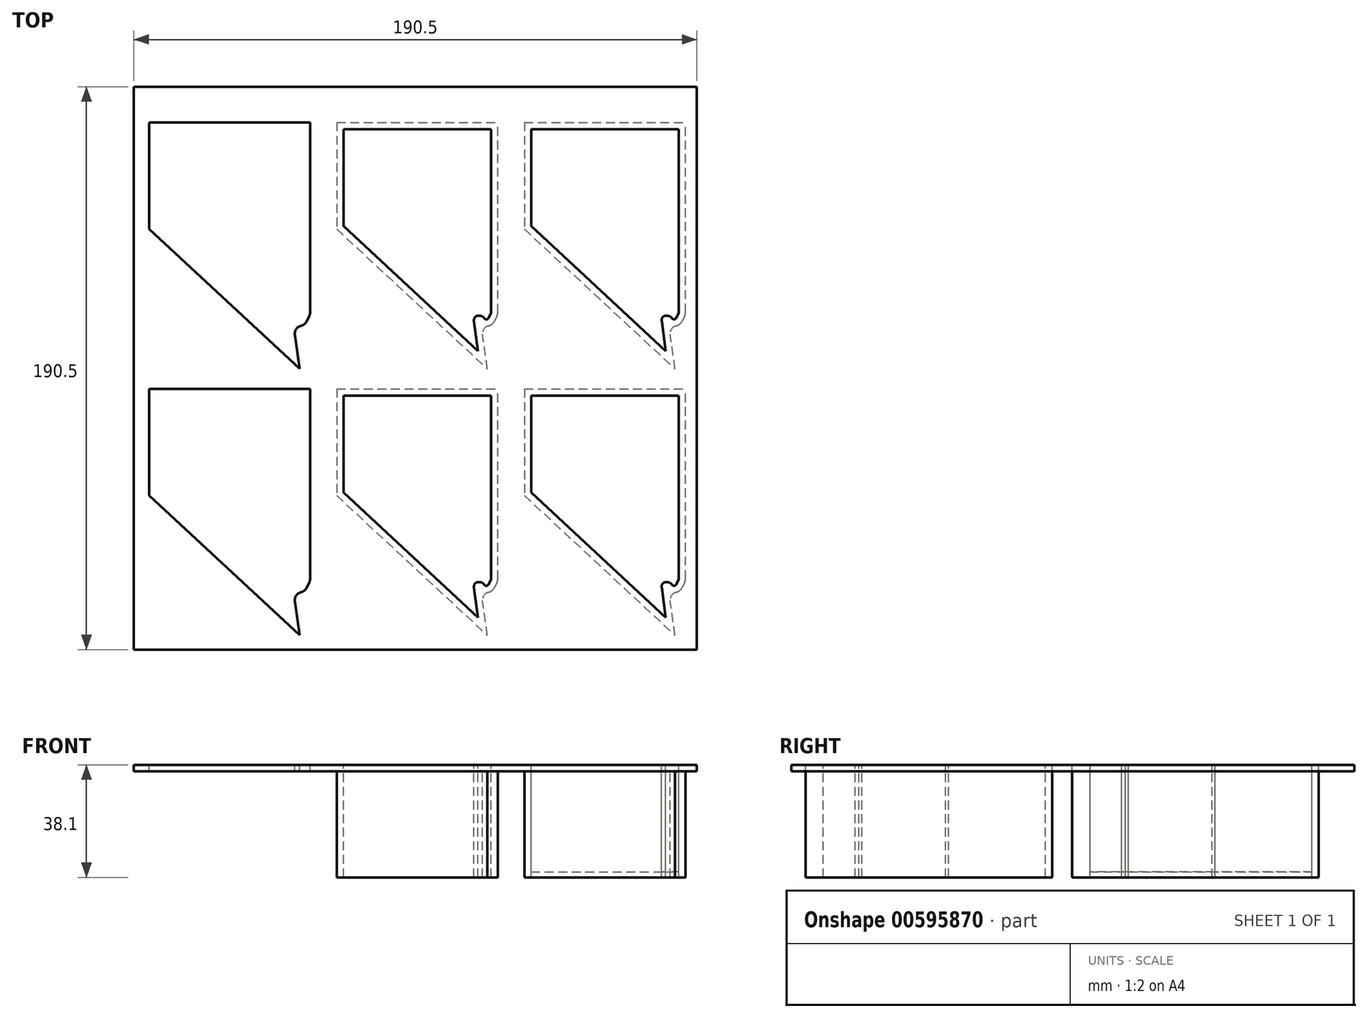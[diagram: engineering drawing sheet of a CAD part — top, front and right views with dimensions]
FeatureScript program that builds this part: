
annotation { "Feature Type Name" : "Feature", "Feature Type Description" : "" }
export const myFeature = defineFeature(function(context is Context, id is Id, definition is map)
    precondition{}
    {
        {
            var Q0;
            Q0=qCreatedBy(makeId("Top.planeOp"),FACE);
            var sketch = newSketch(context, id + "F0", { "sketchPlane" : qUnion([Q0])});
            skLineSegment(sketch, "E0.bottom", {"start": v(-114.3, -95.25) * mm, "end": v(76.2, -95.25) * mm});
            skLineSegment(sketch, "E0.top", {"start": v(-114.3, 95.25) * mm, "end": v(76.2, 95.25) * mm});
            skLineSegment(sketch, "E0.left", {"start": v(-114.3, -95.25) * mm, "end": v(-114.3, 95.25) * mm});
            skLineSegment(sketch, "E0.right", {"start": v(76.2, -95.25) * mm, "end": v(76.2, 95.25) * mm});
            skLineSegment(sketch, "E1", {"start": v(20.1, 80.88) * mm, "end": v(20.1, 48.05) * mm});
            skLineSegment(sketch, "E2", {"start": v(65.66, 5.75) * mm, "end": v(64.3, 16.05) * mm});
            skLineSegment(sketch, "E3", {"start": v(70.06, 18.75) * mm, "end": v(70.06, 80.88) * mm});
            skLineSegment(sketch, "E4", {"start": v(20.1, 80.88) * mm, "end": v(70.06, 80.88) * mm});
            skLineSegment(sketch, "E5", {"start": v(20.1, 48.05) * mm, "end": v(65.66, 5.75) * mm});
            skLineSegment(sketch, "E6", {"start": v(65.58, 17.73) * mm, "end": v(65.7, 17.75) * mm});
            skLineSegment(sketch, "E7", {"start": v(67.72, 17) * mm, "end": v(67.97, 16.73) * mm});
            skLineSegment(sketch, "E8", {"start": v(70.06, 18.75) * mm, "end": v(69.13, 16.89) * mm});
            skPoint(sketch, "E9.visualSharp", {"position": v(64.1, 17.54) * mm});
            skArc(sketch, "E9.filletArc", {"start": v(65.58, 17.73) * mm, "mid": v(64.6, 17.16) * mm, "end": v(64.3, 16.05) * mm});
            skPoint(sketch, "E10.visualSharp", {"position": v(66.9, 17.9) * mm});
            skArc(sketch, "E10.filletArc", {"start": v(67.72, 17) * mm, "mid": v(66.8, 17.62) * mm, "end": v(65.7, 17.75) * mm});
            skPoint(sketch, "E11.visualSharp", {"position": v(68.67, 15.95) * mm});
            skArc(sketch, "E11.filletArc", {"start": v(67.97, 16.73) * mm, "mid": v(68.6, 16.5) * mm, "end": v(69.13, 16.89) * mm});
            skLineSegment(sketch, "E12.0", {"start": v(17.82, 47.06) * mm, "end": v(68.76, -0.25) * mm});
            skLineSegment(sketch, "E12.1", {"start": v(17.82, 83.17) * mm, "end": v(17.82, 47.06) * mm});
            skArc(sketch, "E12.2", {"start": v(69.16, 14.28) * mm, "mid": v(70.35, 14.85) * mm, "end": v(71.18, 15.87) * mm});
            skLineSegment(sketch, "E12.3", {"start": v(72.08, 17.68) * mm, "end": v(71.18, 15.87) * mm});
            skLineSegment(sketch, "E12.4", {"start": v(72.34, 18.81) * mm, "end": v(72.34, 83.17) * mm});
            skLineSegment(sketch, "E12.5", {"start": v(68.76, -0.25) * mm, "end": v(67.21, 11.47) * mm});
            skLineSegment(sketch, "E12.6", {"start": v(17.82, 83.17) * mm, "end": v(72.34, 83.17) * mm});
            skPoint(sketch, "E13.visualSharp", {"position": v(66.78, 14.75) * mm});
            skArc(sketch, "E13.filletArc", {"start": v(69.16, 14.28) * mm, "mid": v(67.64, 13.26) * mm, "end": v(67.21, 11.47) * mm});
            skPoint(sketch, "E14.visualSharp", {"position": v(72.34, 18.22) * mm});
            skArc(sketch, "E14.filletArc", {"start": v(72.08, 17.68) * mm, "mid": v(72.28, 18.23) * mm, "end": v(72.34, 18.81) * mm});
            skLineSegment(sketch, "E15.0.1.0", {"start": v(20.1, -42.12) * mm, "end": v(65.66, -84.42) * mm});
            skLineSegment(sketch, "E15.0.1.1", {"start": v(70.06, -71.42) * mm, "end": v(70.06, -9.29) * mm});
            skLineSegment(sketch, "E15.0.1.2", {"start": v(20.1, -9.29) * mm, "end": v(20.1, -42.12) * mm});
            skLineSegment(sketch, "E15.0.1.3", {"start": v(72.34, -71.36) * mm, "end": v(72.34, -7) * mm});
            skLineSegment(sketch, "E15.0.1.4", {"start": v(17.82, -7) * mm, "end": v(72.34, -7) * mm});
            skLineSegment(sketch, "E15.0.1.5", {"start": v(17.82, -7) * mm, "end": v(17.82, -43.11) * mm});
            skLineSegment(sketch, "E15.0.1.6", {"start": v(20.1, -9.29) * mm, "end": v(70.06, -9.29) * mm});
            skLineSegment(sketch, "E15.0.1.7", {"start": v(17.82, -43.11) * mm, "end": v(68.76, -90.42) * mm});
            skLineSegment(sketch, "E15.0.1.8", {"start": v(68.76, -90.42) * mm, "end": v(67.21, -78.7) * mm});
            skPoint(sketch, "E15.0.1.9", {"position": v(66.78, -75.42) * mm});
            skPoint(sketch, "E15.0.1.10", {"position": v(64.1, -72.63) * mm});
            skLineSegment(sketch, "E15.0.1.11", {"start": v(65.66, -84.42) * mm, "end": v(64.3, -74.12) * mm});
            skPoint(sketch, "E15.0.1.12", {"position": v(66.9, -72.26) * mm});
            skPoint(sketch, "E15.0.1.13", {"position": v(68.67, -74.22) * mm});
            skPoint(sketch, "E15.0.1.14", {"position": v(72.34, -71.95) * mm});
            skArc(sketch, "E15.0.1.15", {"start": v(69.16, -75.89) * mm, "mid": v(67.64, -76.91) * mm, "end": v(67.21, -78.7) * mm});
            skArc(sketch, "E15.0.1.16", {"start": v(72.08, -72.49) * mm, "mid": v(72.28, -71.94) * mm, "end": v(72.34, -71.36) * mm});
            skLineSegment(sketch, "E15.0.1.17", {"start": v(72.08, -72.49) * mm, "end": v(71.18, -74.3) * mm});
            skArc(sketch, "E15.0.1.18", {"start": v(69.16, -75.89) * mm, "mid": v(70.35, -75.32) * mm, "end": v(71.18, -74.3) * mm});
            skLineSegment(sketch, "E15.0.1.19", {"start": v(67.72, -73.17) * mm, "end": v(67.97, -73.44) * mm});
            skLineSegment(sketch, "E15.0.1.20", {"start": v(70.06, -71.42) * mm, "end": v(69.13, -73.28) * mm});
            skArc(sketch, "E15.0.1.21", {"start": v(67.97, -73.44) * mm, "mid": v(68.6, -73.67) * mm, "end": v(69.13, -73.28) * mm});
            skArc(sketch, "E15.0.1.22", {"start": v(67.72, -73.17) * mm, "mid": v(66.8, -72.55) * mm, "end": v(65.7, -72.42) * mm});
            skArc(sketch, "E15.0.1.23", {"start": v(65.58, -72.44) * mm, "mid": v(64.6, -73.01) * mm, "end": v(64.3, -74.12) * mm});
            skLineSegment(sketch, "E15.0.1.24", {"start": v(65.58, -72.44) * mm, "end": v(65.7, -72.42) * mm});
            skLineSegment(sketch, "E15.1.0.0", {"start": v(-43.4, 48.05) * mm, "end": v(2.16, 5.75) * mm});
            skLineSegment(sketch, "E15.1.0.1", {"start": v(6.56, 18.75) * mm, "end": v(6.56, 80.88) * mm});
            skLineSegment(sketch, "E15.1.0.2", {"start": v(-43.4, 80.88) * mm, "end": v(-43.4, 48.05) * mm});
            skLineSegment(sketch, "E15.1.0.3", {"start": v(8.84, 18.81) * mm, "end": v(8.84, 83.17) * mm});
            skLineSegment(sketch, "E15.1.0.4", {"start": v(-45.68, 83.17) * mm, "end": v(8.84, 83.17) * mm});
            skLineSegment(sketch, "E15.1.0.5", {"start": v(-45.68, 83.17) * mm, "end": v(-45.68, 47.06) * mm});
            skLineSegment(sketch, "E15.1.0.6", {"start": v(-43.4, 80.88) * mm, "end": v(6.56, 80.88) * mm});
            skLineSegment(sketch, "E15.1.0.7", {"start": v(-45.68, 47.06) * mm, "end": v(5.26, -0.25) * mm});
            skLineSegment(sketch, "E15.1.0.8", {"start": v(5.26, -0.25) * mm, "end": v(3.71, 11.47) * mm});
            skPoint(sketch, "E15.1.0.9", {"position": v(3.28, 14.75) * mm});
            skPoint(sketch, "E15.1.0.10", {"position": v(0.6, 17.54) * mm});
            skLineSegment(sketch, "E15.1.0.11", {"start": v(2.16, 5.75) * mm, "end": v(0.8, 16.05) * mm});
            skPoint(sketch, "E15.1.0.12", {"position": v(3.4, 17.9) * mm});
            skPoint(sketch, "E15.1.0.13", {"position": v(5.17, 15.95) * mm});
            skPoint(sketch, "E15.1.0.14", {"position": v(8.84, 18.22) * mm});
            skArc(sketch, "E15.1.0.15", {"start": v(5.66, 14.28) * mm, "mid": v(4.14, 13.26) * mm, "end": v(3.71, 11.47) * mm});
            skArc(sketch, "E15.1.0.16", {"start": v(8.58, 17.68) * mm, "mid": v(8.78, 18.23) * mm, "end": v(8.84, 18.81) * mm});
            skLineSegment(sketch, "E15.1.0.17", {"start": v(8.58, 17.68) * mm, "end": v(7.68, 15.87) * mm});
            skArc(sketch, "E15.1.0.18", {"start": v(5.66, 14.28) * mm, "mid": v(6.85, 14.85) * mm, "end": v(7.68, 15.87) * mm});
            skLineSegment(sketch, "E15.1.0.19", {"start": v(4.22, 17) * mm, "end": v(4.47, 16.73) * mm});
            skLineSegment(sketch, "E15.1.0.20", {"start": v(6.56, 18.75) * mm, "end": v(5.63, 16.89) * mm});
            skArc(sketch, "E15.1.0.21", {"start": v(4.47, 16.73) * mm, "mid": v(5.1, 16.5) * mm, "end": v(5.63, 16.89) * mm});
            skArc(sketch, "E15.1.0.22", {"start": v(4.22, 17) * mm, "mid": v(3.3, 17.62) * mm, "end": v(2.2, 17.75) * mm});
            skArc(sketch, "E15.1.0.23", {"start": v(2.08, 17.73) * mm, "mid": v(1.1, 17.16) * mm, "end": v(0.8, 16.05) * mm});
            skLineSegment(sketch, "E15.1.0.24", {"start": v(2.08, 17.73) * mm, "end": v(2.2, 17.75) * mm});
            skLineSegment(sketch, "E15.1.1.0", {"start": v(-43.4, -42.12) * mm, "end": v(2.16, -84.42) * mm});
            skLineSegment(sketch, "E15.1.1.1", {"start": v(6.56, -71.42) * mm, "end": v(6.56, -9.29) * mm});
            skLineSegment(sketch, "E15.1.1.2", {"start": v(-43.4, -9.29) * mm, "end": v(-43.4, -42.12) * mm});
            skLineSegment(sketch, "E15.1.1.3", {"start": v(8.84, -71.36) * mm, "end": v(8.84, -7) * mm});
            skLineSegment(sketch, "E15.1.1.4", {"start": v(-45.68, -7) * mm, "end": v(8.84, -7) * mm});
            skLineSegment(sketch, "E15.1.1.5", {"start": v(-45.68, -7) * mm, "end": v(-45.68, -43.11) * mm});
            skLineSegment(sketch, "E15.1.1.6", {"start": v(-43.4, -9.29) * mm, "end": v(6.56, -9.29) * mm});
            skLineSegment(sketch, "E15.1.1.7", {"start": v(-45.68, -43.11) * mm, "end": v(5.26, -90.42) * mm});
            skLineSegment(sketch, "E15.1.1.8", {"start": v(5.26, -90.42) * mm, "end": v(3.71, -78.7) * mm});
            skPoint(sketch, "E15.1.1.9", {"position": v(3.28, -75.42) * mm});
            skPoint(sketch, "E15.1.1.10", {"position": v(0.6, -72.63) * mm});
            skLineSegment(sketch, "E15.1.1.11", {"start": v(2.16, -84.42) * mm, "end": v(0.8, -74.12) * mm});
            skPoint(sketch, "E15.1.1.12", {"position": v(3.4, -72.26) * mm});
            skPoint(sketch, "E15.1.1.13", {"position": v(5.17, -74.22) * mm});
            skPoint(sketch, "E15.1.1.14", {"position": v(8.84, -71.95) * mm});
            skArc(sketch, "E15.1.1.15", {"start": v(5.66, -75.89) * mm, "mid": v(4.14, -76.91) * mm, "end": v(3.71, -78.7) * mm});
            skArc(sketch, "E15.1.1.16", {"start": v(8.58, -72.49) * mm, "mid": v(8.78, -71.94) * mm, "end": v(8.84, -71.36) * mm});
            skLineSegment(sketch, "E15.1.1.17", {"start": v(8.58, -72.49) * mm, "end": v(7.68, -74.3) * mm});
            skArc(sketch, "E15.1.1.18", {"start": v(5.66, -75.89) * mm, "mid": v(6.85, -75.32) * mm, "end": v(7.68, -74.3) * mm});
            skLineSegment(sketch, "E15.1.1.19", {"start": v(4.22, -73.17) * mm, "end": v(4.47, -73.44) * mm});
            skLineSegment(sketch, "E15.1.1.20", {"start": v(6.56, -71.42) * mm, "end": v(5.63, -73.28) * mm});
            skArc(sketch, "E15.1.1.21", {"start": v(4.47, -73.44) * mm, "mid": v(5.1, -73.67) * mm, "end": v(5.63, -73.28) * mm});
            skArc(sketch, "E15.1.1.22", {"start": v(4.22, -73.17) * mm, "mid": v(3.3, -72.55) * mm, "end": v(2.2, -72.42) * mm});
            skArc(sketch, "E15.1.1.23", {"start": v(2.08, -72.44) * mm, "mid": v(1.1, -73.01) * mm, "end": v(0.8, -74.12) * mm});
            skLineSegment(sketch, "E15.1.1.24", {"start": v(2.08, -72.44) * mm, "end": v(2.2, -72.42) * mm});
            skLineSegment(sketch, "E15.direction1", {"start": v(17.82, 47.06) * mm, "end": v(-45.68, 47.06) * mm, "construction": true});
            skLineSegment(sketch, "E15.direction2", {"start": v(17.82, 47.06) * mm, "end": v(17.82, -43.11) * mm, "construction": true});
            skLineSegment(sketch, "E16.0.2.0", {"start": v(-106.9, 48.05) * mm, "end": v(-61.34, 5.75) * mm});
            skLineSegment(sketch, "E16.3.2.0", {"start": v(-56.94, 18.75) * mm, "end": v(-56.94, 80.88) * mm});
            skLineSegment(sketch, "E16.6.2.0", {"start": v(-106.9, 80.88) * mm, "end": v(-106.9, 48.05) * mm});
            skLineSegment(sketch, "E16.9.2.0", {"start": v(-54.66, 18.81) * mm, "end": v(-54.66, 83.17) * mm});
            skLineSegment(sketch, "E16.12.2.0", {"start": v(-109.18, 83.17) * mm, "end": v(-54.66, 83.17) * mm});
            skLineSegment(sketch, "E16.15.2.0", {"start": v(-109.18, 83.17) * mm, "end": v(-109.18, 47.06) * mm});
            skLineSegment(sketch, "E16.18.2.0", {"start": v(-106.9, 80.88) * mm, "end": v(-56.94, 80.88) * mm});
            skLineSegment(sketch, "E16.21.2.0", {"start": v(-109.18, 47.06) * mm, "end": v(-58.24, -0.25) * mm});
            skLineSegment(sketch, "E16.24.2.0", {"start": v(-58.24, -0.25) * mm, "end": v(-59.79, 11.47) * mm});
            skPoint(sketch, "E16.27.2.0", {"position": v(-60.22, 14.75) * mm});
            skPoint(sketch, "E16.28.2.0", {"position": v(-62.9, 17.54) * mm});
            skLineSegment(sketch, "E16.29.2.0", {"start": v(-61.34, 5.75) * mm, "end": v(-62.7, 16.05) * mm});
            skPoint(sketch, "E16.32.2.0", {"position": v(-60.1, 17.9) * mm});
            skPoint(sketch, "E16.33.2.0", {"position": v(-58.33, 15.95) * mm});
            skPoint(sketch, "E16.34.2.0", {"position": v(-54.66, 18.22) * mm});
            skArc(sketch, "E16.35.2.0", {"start": v(-57.84, 14.28) * mm, "mid": v(-59.36, 13.26) * mm, "end": v(-59.79, 11.47) * mm});
            skArc(sketch, "E16.39.2.0", {"start": v(-54.92, 17.68) * mm, "mid": v(-54.72, 18.23) * mm, "end": v(-54.66, 18.81) * mm});
            skLineSegment(sketch, "E16.43.2.0", {"start": v(-54.92, 17.68) * mm, "end": v(-55.82, 15.87) * mm});
            skArc(sketch, "E16.46.2.0", {"start": v(-57.84, 14.28) * mm, "mid": v(-56.65, 14.85) * mm, "end": v(-55.82, 15.87) * mm});
            skLineSegment(sketch, "E16.50.2.0", {"start": v(-59.28, 17) * mm, "end": v(-59.03, 16.73) * mm});
            skLineSegment(sketch, "E16.53.2.0", {"start": v(-56.94, 18.75) * mm, "end": v(-57.87, 16.89) * mm});
            skArc(sketch, "E16.56.2.0", {"start": v(-59.03, 16.73) * mm, "mid": v(-58.4, 16.5) * mm, "end": v(-57.87, 16.89) * mm});
            skArc(sketch, "E16.60.2.0", {"start": v(-59.28, 17) * mm, "mid": v(-60.2, 17.62) * mm, "end": v(-61.3, 17.75) * mm});
            skArc(sketch, "E16.64.2.0", {"start": v(-61.42, 17.73) * mm, "mid": v(-62.4, 17.16) * mm, "end": v(-62.7, 16.05) * mm});
            skLineSegment(sketch, "E16.68.2.0", {"start": v(-61.42, 17.73) * mm, "end": v(-61.3, 17.75) * mm});
            skLineSegment(sketch, "E16.0.2.1", {"start": v(-106.9, -42.12) * mm, "end": v(-61.34, -84.42) * mm});
            skLineSegment(sketch, "E16.3.2.1", {"start": v(-56.94, -71.42) * mm, "end": v(-56.94, -9.29) * mm});
            skLineSegment(sketch, "E16.6.2.1", {"start": v(-106.9, -9.29) * mm, "end": v(-106.9, -42.12) * mm});
            skLineSegment(sketch, "E16.9.2.1", {"start": v(-54.66, -71.36) * mm, "end": v(-54.66, -7) * mm});
            skLineSegment(sketch, "E16.12.2.1", {"start": v(-109.18, -7) * mm, "end": v(-54.66, -7) * mm});
            skLineSegment(sketch, "E16.15.2.1", {"start": v(-109.18, -7) * mm, "end": v(-109.18, -43.11) * mm});
            skLineSegment(sketch, "E16.18.2.1", {"start": v(-106.9, -9.29) * mm, "end": v(-56.94, -9.29) * mm});
            skLineSegment(sketch, "E16.21.2.1", {"start": v(-109.18, -43.11) * mm, "end": v(-58.24, -90.42) * mm});
            skLineSegment(sketch, "E16.24.2.1", {"start": v(-58.24, -90.42) * mm, "end": v(-59.79, -78.7) * mm});
            skPoint(sketch, "E16.27.2.1", {"position": v(-60.22, -75.42) * mm});
            skPoint(sketch, "E16.28.2.1", {"position": v(-62.9, -72.63) * mm});
            skLineSegment(sketch, "E16.29.2.1", {"start": v(-61.34, -84.42) * mm, "end": v(-62.7, -74.12) * mm});
            skPoint(sketch, "E16.32.2.1", {"position": v(-60.1, -72.26) * mm});
            skPoint(sketch, "E16.33.2.1", {"position": v(-58.33, -74.22) * mm});
            skPoint(sketch, "E16.34.2.1", {"position": v(-54.66, -71.95) * mm});
            skArc(sketch, "E16.35.2.1", {"start": v(-57.84, -75.89) * mm, "mid": v(-59.36, -76.91) * mm, "end": v(-59.79, -78.7) * mm});
            skArc(sketch, "E16.39.2.1", {"start": v(-54.92, -72.49) * mm, "mid": v(-54.72, -71.94) * mm, "end": v(-54.66, -71.36) * mm});
            skLineSegment(sketch, "E16.43.2.1", {"start": v(-54.92, -72.49) * mm, "end": v(-55.82, -74.3) * mm});
            skArc(sketch, "E16.46.2.1", {"start": v(-57.84, -75.89) * mm, "mid": v(-56.65, -75.32) * mm, "end": v(-55.82, -74.3) * mm});
            skLineSegment(sketch, "E16.50.2.1", {"start": v(-59.28, -73.17) * mm, "end": v(-59.03, -73.44) * mm});
            skLineSegment(sketch, "E16.53.2.1", {"start": v(-56.94, -71.42) * mm, "end": v(-57.87, -73.28) * mm});
            skArc(sketch, "E16.56.2.1", {"start": v(-59.03, -73.44) * mm, "mid": v(-58.4, -73.67) * mm, "end": v(-57.87, -73.28) * mm});
            skArc(sketch, "E16.60.2.1", {"start": v(-59.28, -73.17) * mm, "mid": v(-60.2, -72.55) * mm, "end": v(-61.3, -72.42) * mm});
            skArc(sketch, "E16.64.2.1", {"start": v(-61.42, -72.44) * mm, "mid": v(-62.4, -73.01) * mm, "end": v(-62.7, -74.12) * mm});
            skLineSegment(sketch, "E16.68.2.1", {"start": v(-61.42, -72.44) * mm, "end": v(-61.3, -72.42) * mm});
            skSolve(sketch);
        }
        {
            var Q0;
            Q0=makeQuery(id+"F0.imprint","IMPRINT",FACE,{"disambiguationData":[TD([[makeQuery(id+"F0.imprint","IMPRINT",EDGE,{"derivedFrom":sQuery(id+"F0.wireOp",EDGE,"E15.0.1.0")}),-1.0]])]});
            var Q1;
            Q1=makeQuery(id+"F0.imprint","IMPRINT",FACE,{"disambiguationData":[TD([[makeQuery(id+"F0.imprint","IMPRINT",EDGE,{"derivedFrom":sQuery(id+"F0.wireOp",EDGE,"E1")}),-1.0]])]});
            var Q2;
            Q2=makeQuery(id+"F0.imprint","IMPRINT",FACE,{"disambiguationData":[TD([[makeQuery(id+"F0.imprint","IMPRINT",EDGE,{"derivedFrom":sQuery(id+"F0.wireOp",EDGE,"E15.1.0.0")}),-1.0]])]});
            var Q3;
            Q3=makeQuery(id+"F0.imprint","IMPRINT",FACE,{"disambiguationData":[TD([[makeQuery(id+"F0.imprint","IMPRINT",EDGE,{"derivedFrom":sQuery(id+"F0.wireOp",EDGE,"E15.1.1.0")}),-1.0]])]});
            extrude(context, id + "F1", {"entities" : qUnion([Q0, Q1, Q2, Q3]), "oppositeDirection" : true, "depth" : 38.1 * mm, "offsetDistance" : 25.4 * mm});
        }
        {
            var Q0;
            Q0=makeQuery(id+"F0.imprint","IMPRINT",FACE,{"disambiguationData":[TD([[makeQuery(id+"F0.imprint","IMPRINT",EDGE,{"derivedFrom":sQuery(id+"F0.wireOp",EDGE,"E0.bottom")}),1.0]])]});
            extrude(context, id + "F2", {"entities" : qUnion([Q0]), "operationType" : NewBodyOperationType.ADD, "oppositeDirection" : true, "depth" : 2.16 * mm, "offsetDistance" : 25.4 * mm});
        }
        {
            var Q0;
            Q0=makeQuery(id+"F1.opExtrude","CAP_FACE",FACE,{"disambiguationData":[OSD([sQuery(id+"F0.wireOp",EDGE,"E1"),sQuery(id+"F0.wireOp",EDGE,"E2"),sQuery(id+"F0.wireOp",EDGE,"E3"),sQuery(id+"F0.wireOp",EDGE,"E4"),sQuery(id+"F0.wireOp",EDGE,"E5"),sQuery(id+"F0.wireOp",EDGE,"E6"),sQuery(id+"F0.wireOp",EDGE,"E7"),sQuery(id+"F0.wireOp",EDGE,"E8"),sQuery(id+"F0.wireOp",EDGE,"E9.filletArc"),sQuery(id+"F0.wireOp",EDGE,"E10.filletArc"),sQuery(id+"F0.wireOp",EDGE,"E11.filletArc"),sQuery(id+"F0.wireOp",EDGE,"E12.0"),sQuery(id+"F0.wireOp",EDGE,"E12.1"),sQuery(id+"F0.wireOp",EDGE,"E12.2"),sQuery(id+"F0.wireOp",EDGE,"E12.3"),sQuery(id+"F0.wireOp",EDGE,"E12.4"),sQuery(id+"F0.wireOp",EDGE,"E12.5"),sQuery(id+"F0.wireOp",EDGE,"E12.6"),sQuery(id+"F0.wireOp",EDGE,"E13.filletArc"),sQuery(id+"F0.wireOp",EDGE,"E14.filletArc")])],"isStart":false});
            cPlane(context, id + "F3", {"entities" : qUnion([Q0]), "cplaneType" : CPlaneType.OFFSET, "offset" : 0 * mm, "width" : 152.4 * mm, "height" : 152.4 * mm});
        }
        {
            var Q0;
            Q0=qCreatedBy(id+"F3.planeOp",FACE);
            var sketch = newSketch(context, id + "F4", { "sketchPlane" : qUnion([Q0])});
            skLineSegment(sketch, "E17.0.0", {"start": v(72.08, -17.68) * mm, "end": v(71.18, -15.87) * mm});
            skArc(sketch, "E17.0.1", {"start": v(71.18, -15.87) * mm, "mid": v(70.35, -14.85) * mm, "end": v(69.16, -14.28) * mm});
            skArc(sketch, "E17.0.2", {"start": v(69.16, -14.28) * mm, "mid": v(67.64, -13.26) * mm, "end": v(67.21, -11.47) * mm});
            skLineSegment(sketch, "E17.0.3", {"start": v(67.21, -11.47) * mm, "end": v(68.76, 0.25) * mm});
            skLineSegment(sketch, "E17.0.4", {"start": v(68.76, 0.25) * mm, "end": v(17.82, -47.06) * mm});
            skLineSegment(sketch, "E17.0.5", {"start": v(17.82, -47.06) * mm, "end": v(17.82, -83.17) * mm});
            skLineSegment(sketch, "E17.0.6", {"start": v(17.82, -83.17) * mm, "end": v(72.34, -83.17) * mm});
            skLineSegment(sketch, "E17.0.7", {"start": v(72.34, -83.17) * mm, "end": v(72.34, -18.81) * mm});
            skArc(sketch, "E17.0.8", {"start": v(72.34, -18.81) * mm, "mid": v(72.28, -18.23) * mm, "end": v(72.08, -17.68) * mm});
            skArc(sketch, "E18.0.0", {"start": v(5.66, -14.28) * mm, "mid": v(4.14, -13.26) * mm, "end": v(3.71, -11.47) * mm});
            skLineSegment(sketch, "E18.0.1", {"start": v(3.71, -11.47) * mm, "end": v(5.26, 0.25) * mm});
            skLineSegment(sketch, "E18.0.2", {"start": v(5.26, 0.25) * mm, "end": v(-45.68, -47.06) * mm});
            skLineSegment(sketch, "E18.0.3", {"start": v(-45.68, -47.06) * mm, "end": v(-45.68, -83.17) * mm});
            skLineSegment(sketch, "E18.0.4", {"start": v(-45.68, -83.17) * mm, "end": v(8.84, -83.17) * mm});
            skLineSegment(sketch, "E18.0.5", {"start": v(8.84, -83.17) * mm, "end": v(8.84, -18.81) * mm});
            skArc(sketch, "E18.0.6", {"start": v(8.84, -18.81) * mm, "mid": v(8.78, -18.23) * mm, "end": v(8.58, -17.68) * mm});
            skLineSegment(sketch, "E18.0.7", {"start": v(8.58, -17.68) * mm, "end": v(7.68, -15.87) * mm});
            skArc(sketch, "E18.0.8", {"start": v(7.68, -15.87) * mm, "mid": v(6.85, -14.85) * mm, "end": v(5.66, -14.28) * mm});
            skArc(sketch, "E19.0.0", {"start": v(5.66, 75.89) * mm, "mid": v(4.14, 76.91) * mm, "end": v(3.71, 78.7) * mm});
            skLineSegment(sketch, "E19.0.1", {"start": v(3.71, 78.7) * mm, "end": v(5.26, 90.42) * mm});
            skLineSegment(sketch, "E19.0.2", {"start": v(5.26, 90.42) * mm, "end": v(-45.68, 43.11) * mm});
            skLineSegment(sketch, "E19.0.3", {"start": v(-45.68, 43.11) * mm, "end": v(-45.68, 7) * mm});
            skLineSegment(sketch, "E19.0.4", {"start": v(-45.68, 7) * mm, "end": v(8.84, 7) * mm});
            skLineSegment(sketch, "E19.0.5", {"start": v(8.84, 7) * mm, "end": v(8.84, 71.36) * mm});
            skArc(sketch, "E19.0.6", {"start": v(8.84, 71.36) * mm, "mid": v(8.78, 71.94) * mm, "end": v(8.58, 72.49) * mm});
            skLineSegment(sketch, "E19.0.7", {"start": v(8.58, 72.49) * mm, "end": v(7.68, 74.3) * mm});
            skArc(sketch, "E19.0.8", {"start": v(7.68, 74.3) * mm, "mid": v(6.85, 75.32) * mm, "end": v(5.66, 75.89) * mm});
            skArc(sketch, "E20.0.0", {"start": v(69.16, 75.89) * mm, "mid": v(67.64, 76.91) * mm, "end": v(67.21, 78.7) * mm});
            skLineSegment(sketch, "E20.0.1", {"start": v(67.21, 78.7) * mm, "end": v(68.76, 90.42) * mm});
            skLineSegment(sketch, "E20.0.2", {"start": v(68.76, 90.42) * mm, "end": v(17.82, 43.11) * mm});
            skLineSegment(sketch, "E20.0.3", {"start": v(17.82, 43.11) * mm, "end": v(17.82, 7) * mm});
            skLineSegment(sketch, "E20.0.4", {"start": v(17.82, 7) * mm, "end": v(72.34, 7) * mm});
            skLineSegment(sketch, "E20.0.5", {"start": v(72.34, 7) * mm, "end": v(72.34, 71.36) * mm});
            skArc(sketch, "E20.0.6", {"start": v(72.34, 71.36) * mm, "mid": v(72.28, 71.94) * mm, "end": v(72.08, 72.49) * mm});
            skLineSegment(sketch, "E20.0.7", {"start": v(72.08, 72.49) * mm, "end": v(71.18, 74.3) * mm});
            skArc(sketch, "E20.0.8", {"start": v(71.18, 74.3) * mm, "mid": v(70.35, 75.32) * mm, "end": v(69.16, 75.89) * mm});
            skSolve(sketch);
        }
        {
            var Q0;
            Q0=makeQuery(id+"F4.imprint","IMPRINT",FACE,{"disambiguationData":[TD([[makeQuery(id+"F4.imprint","IMPRINT",EDGE,{"derivedFrom":sQuery(id+"F4.wireOp",EDGE,"E17.0.0")}),1.0]])]});
            var Q1;
            Q1=makeQuery(id+"F4.imprint","IMPRINT",FACE,{"disambiguationData":[TD([[makeQuery(id+"F4.imprint","IMPRINT",EDGE,{"derivedFrom":sQuery(id+"F4.wireOp",EDGE,"E18.0.0")}),1.0]])]});
            var Q2;
            Q2=makeQuery(id+"F4.imprint","IMPRINT",FACE,{"disambiguationData":[TD([[makeQuery(id+"F4.imprint","IMPRINT",EDGE,{"derivedFrom":sQuery(id+"F4.wireOp",EDGE,"E20.0.0")}),1.0]])]});
            var Q3;
            Q3=makeQuery(id+"F4.imprint","IMPRINT",FACE,{"disambiguationData":[TD([[makeQuery(id+"F4.imprint","IMPRINT",EDGE,{"derivedFrom":sQuery(id+"F4.wireOp",EDGE,"E19.0.0")}),1.0]])]});
            extrude(context, id + "F5", {"entities" : qUnion([Q0, Q1, Q2, Q3]), "operationType" : NewBodyOperationType.ADD, "oppositeDirection" : true, "depth" : 1.9 * mm, "offsetDistance" : 25.4 * mm});
        }
    });
